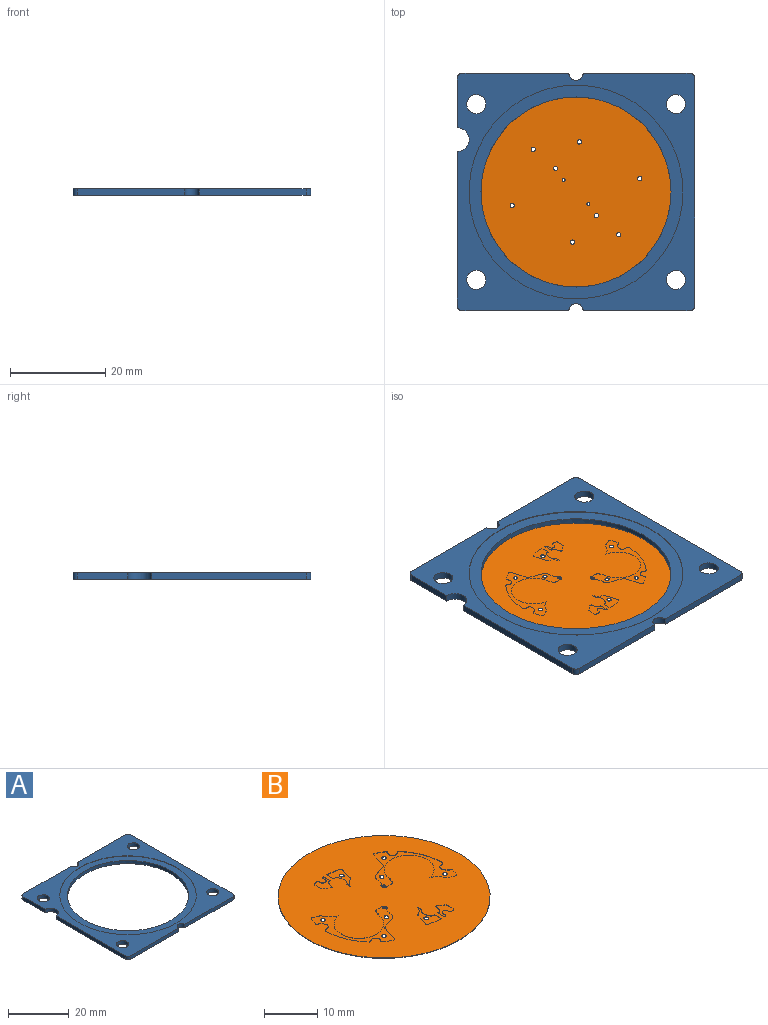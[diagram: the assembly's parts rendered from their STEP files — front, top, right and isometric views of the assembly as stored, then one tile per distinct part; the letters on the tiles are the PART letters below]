
ASSEMBLY  parts=2 mates=1
PART A: 23 faces, bbox 50x50x1.4 mm
  f0: plane 48x1.4mm, normal (1,0,0), area 67.2mm2, adj f1,f17,f18,f19
  f1: cylinder r=1mm len=1.4mm, axis (0,0,-1), area 2.2mm2, adj f0,f2,f18,f19
  f2: plane 22.5x1.4mm, normal (0,1,0), area 31.5mm2, adj f1,f3,f18,f19
  f3: cylinder r=1.5mm len=3mm, axis (0,0,-1), area 6.6mm2, adj f2,f4,f18,f19
  f4: plane 22.5x1.4mm, normal (0,1,0), area 31.5mm2, adj f3,f5,f18,f19
  f5: cylinder r=1mm len=1.4mm, axis (0,0,-1), area 2.2mm2, adj f4,f6,f18,f19
  f6: plane 10.5x1.4mm, normal (-1,0,0), area 14.7mm2, adj f5,f7,f18,f19
  f7: cylinder r=2.5mm len=5mm, axis (0,0,-1), area 11mm2, adj f6,f8,f18,f19
  f8: plane 32.5x1.4mm, normal (-1,0,0), area 45.5mm2, adj f7,f9,f18,f19
  f9: cylinder r=1mm len=1.4mm, axis (0,0,-1), area 2.2mm2, adj f8,f10,f18,f19
  f10: plane 22.5x1.4mm, normal (0,-1,0), area 31.5mm2, adj f9,f11,f18,f19
  f11: cylinder r=1.5mm len=3mm, axis (0,0,-1), area 6.6mm2, adj f10,f12,f18,f19
  f12: plane 22.5x1.4mm, normal (0,-1,0), area 31.5mm2, adj f11,f17,f18,f19
  f13: cylinder r=2mm len=4.01mm, axis (0,0,-1), area 17.6mm2, adj f18,f19
  f14: cylinder r=2mm len=4.01mm, axis (0,0,-1), area 17.6mm2, adj f18,f19
  f15: cylinder r=2mm len=4.01mm, axis (0,0,-1), area 17.6mm2, adj f18,f19
  f16: cylinder r=2mm len=4.01mm, axis (0,0,-1), area 17.6mm2, adj f18,f19
  f17: cylinder r=1mm len=1.4mm, axis (0,0,-1), area 2.2mm2, adj f0,f12,f18,f19
  f18: plane 50x50mm, normal (0,0,1), area 841.3mm2, adj f0,f1,f2,f3,f4,f5,f6,f7
  f19: plane 50x50mm, normal (0,0,-1), area 1175.1mm2, adj f0,f1,f2,f3,f4,f5,f6,f7
  f20: cylinder r=22.5mm len=45mm, axis (0,0,1), area 17mm2, adj f18,f21
  f21: plane 45x45mm, normal (0,0,1), area 333.8mm2, adj f20,f22
  f22: cylinder r=20mm len=40mm, axis (0,0,-1), area 160.8mm2, adj f19,f21
PART B: 127 faces, bbox 40x40x0.1 mm
  f0: plane 40x40mm, normal (0,0,1), area 1136.6mm2, adj f11,f13,f14,f15,f16,f17,f18,f19
  f1: cylinder r=0.45mm len=0.91mm, axis (0,0,1), area 0.1mm2, adj f12,f92
  f2: cylinder r=0.45mm len=0.91mm, axis (0,0,1), area 0.1mm2, adj f12,f92
  f3: cylinder r=0.45mm len=0.89mm, axis (0,0,1), area 0.1mm2, adj f12,f92
  f4: cylinder r=0.3mm len=0.6mm, axis (0,0,1), area 0.1mm2, adj f12,f92
  f5: cylinder r=0.45mm len=0.91mm, axis (0,0,1), area 0.1mm2, adj f12,f63
  f6: cylinder r=0.3mm len=0.6mm, axis (0,0,1), area 0.1mm2, adj f12,f52
  f7: cylinder r=0.45mm len=0.89mm, axis (0,0,1), area 0.1mm2, adj f12,f52
  f8: cylinder r=0.45mm len=0.91mm, axis (0,0,1), area 0.1mm2, adj f12,f52
  f9: cylinder r=0.45mm len=0.91mm, axis (0,0,1), area 0.1mm2, adj f12,f52
  f10: cylinder r=0.45mm len=0.91mm, axis (0,0,1), area 0.1mm2, adj f12,f23
  f11: cylinder r=20mm len=40mm, axis (0,0,-1), area 12.6mm2, adj f0,f12
  f12: plane 40x40mm, normal (0,0,-1), area 1250.9mm2, adj f1,f2,f3,f4,f5,f6,f7,f8
  f13: cylinder r=0.4mm len=0.5mm, axis (0,0,1), area 0mm2, adj f0,f14,f22,f23
  f14: cylinder r=12.7mm len=3.01mm, axis (0,0,1), area 0.2mm2, adj f0,f13,f15,f23
  f15: plane 1.88x0.05mm, normal (1,0,0), area 0.1mm2, adj f0,f14,f16,f23
  f16: cylinder r=0.65mm len=0.91mm, axis (0,0,1), area 0.1mm2, adj f0,f15,f17,f23
  f17: cylinder r=1.65mm len=2.34mm, axis (0,0,1), area 0.1mm2, adj f0,f16,f18,f23
  f18: cylinder r=1.25mm len=0.75mm, axis (0,0,1), area 0mm2, adj f0,f17,f19,f23
  f19: cylinder r=1.25mm len=0.15mm, axis (0,0,1), area 0mm2, adj f0,f18,f20,f23
  f20: cylinder r=2.8mm len=1.64mm, axis (0,0,1), area 0.1mm2, adj f0,f19,f21,f23
  f21: cylinder r=0.6mm len=0.37mm, axis (0,0,1), area 0mm2, adj f0,f20,f22,f23
  f22: plane 2.75x0.85mm, normal (-0.96,0.3,0), area 0.1mm2, adj f0,f13,f21,f23
  f23: plane 5.73x3.3mm, normal (0,0,1), area 9mm2, adj f10,f13,f14,f15,f16,f17,f18,f19
  f24: cylinder r=4.7mm len=9.39mm, axis (0,0,1), area 1mm2, adj f0,f25,f51,f52
  f25: cylinder r=4.7mm len=2.54mm, axis (0,0,1), area 0.2mm2, adj f0,f24,f26,f52
  f26: cylinder r=0.6mm len=0.37mm, axis (0,0,1), area 0mm2, adj f0,f25,f27,f52
  f27: plane 1.09x0.49mm, normal (-0.41,-0.91,0), area 0.1mm2, adj f0,f26,f28,f52
  f28: cylinder r=0.4mm len=0.54mm, axis (0,0,1), area 0mm2, adj f0,f27,f29,f52
  f29: cylinder r=12.7mm len=1.65mm, axis (0,0,1), area 0.1mm2, adj f0,f28,f30,f52
  f30: cylinder r=0.3mm len=0.37mm, axis (0,0,1), area 0mm2, adj f0,f29,f31,f52
  f31: cylinder r=0.5mm len=0.47mm, axis (0,0,1), area 0mm2, adj f0,f30,f32,f52
  f32: plane 0.67x0.39mm, normal (0.86,0.5,0), area 0mm2, adj f0,f31,f33,f52
  f33: cylinder r=0.85mm len=1.28mm, axis (0,0,1), area 0.1mm2, adj f0,f32,f34,f52
  f34: cylinder r=0.5mm len=0.6mm, axis (0,0,1), area 0mm2, adj f0,f33,f35,f52
  f35: cylinder r=12.7mm len=8.29mm, axis (0,0,1), area 0.5mm2, adj f0,f34,f36,f52
  f36: cylinder r=0.3mm len=0.45mm, axis (0,0,1), area 0mm2, adj f0,f35,f37,f52
  f37: cylinder r=0.9mm len=1.58mm, axis (0,0,1), area 0.1mm2, adj f0,f36,f38,f52
  f38: cylinder r=0.3mm len=0.45mm, axis (0,0,1), area 0mm2, adj f0,f37,f39,f52
  f39: cylinder r=12.7mm len=1.81mm, axis (0,0,1), area 0.1mm2, adj f0,f38,f40,f52
  f40: cylinder r=0.4mm len=0.57mm, axis (0,0,1), area 0mm2, adj f0,f39,f41,f52
  f41: plane 3.64x1.14mm, normal (-0.95,0.3,0), area 0.2mm2, adj f0,f40,f42,f52
  f42: cylinder r=0.4mm len=0.26mm, axis (0,0,1), area 0mm2, adj f0,f41,f43,f52
  f43: plane 2.98x1.06mm, normal (-0.34,0.94,0), area 0.2mm2, adj f0,f42,f44,f52
  f44: cylinder r=1.2mm len=1.02mm, axis (0,0,1), area 0.1mm2, adj f0,f43,f45,f52
  f45: cylinder r=5mm len=1.73mm, axis (0,0,1), area 0.1mm2, adj f0,f44,f46,f52
  f46: cylinder r=0.4mm len=0.24mm, axis (0,0,1), area 0mm2, adj f0,f45,f47,f52
  f47: cylinder r=0.6mm len=1.17mm, axis (0,0,1), area 0.1mm2, adj f0,f46,f48,f52
  f48: plane 1.33x0.05mm, normal (0.01,-1,0), area 0.1mm2, adj f0,f47,f49,f52
  f49: cylinder r=0.7mm len=0.67mm, axis (0,0,1), area 0mm2, adj f0,f48,f50,f52
  f50: plane 0.54x0.13mm, normal (0.97,-0.24,0), area 0mm2, adj f0,f49,f51,f52
  f51: cylinder r=0.4mm len=0.27mm, axis (0,0,1), area 0mm2, adj f0,f24,f50,f52
  f52: plane 16.09x13.73mm, normal (0,0,1), area 42mm2, adj f6,f7,f8,f9,f24,f25,f26,f27
  f53: cylinder r=0.4mm len=0.5mm, axis (0,0,1), area 0mm2, adj f0,f54,f62,f63
  f54: cylinder r=12.7mm len=3.01mm, axis (0,0,1), area 0.2mm2, adj f0,f53,f55,f63
  f55: plane 1.88x0.05mm, normal (-1,0,0), area 0.1mm2, adj f0,f54,f56,f63
  f56: cylinder r=0.65mm len=0.91mm, axis (0,0,1), area 0.1mm2, adj f0,f55,f57,f63
  f57: cylinder r=1.65mm len=2.34mm, axis (0,0,1), area 0.1mm2, adj f0,f56,f58,f63
  f58: cylinder r=1.25mm len=0.75mm, axis (0,0,1), area 0mm2, adj f0,f57,f59,f63
  f59: cylinder r=1.25mm len=0.15mm, axis (0,0,1), area 0mm2, adj f0,f58,f60,f63
  f60: cylinder r=2.8mm len=1.64mm, axis (0,0,1), area 0.1mm2, adj f0,f59,f61,f63
  f61: cylinder r=0.6mm len=0.37mm, axis (0,0,1), area 0mm2, adj f0,f60,f62,f63
  f62: plane 2.75x0.85mm, normal (0.96,-0.3,0), area 0.1mm2, adj f0,f53,f61,f63
  f63: plane 5.73x3.3mm, normal (0,0,1), area 9mm2, adj f5,f53,f54,f55,f56,f57,f58,f59
  f64: cylinder r=4.7mm len=9.39mm, axis (0,0,1), area 1mm2, adj f0,f65,f91,f92
  f65: cylinder r=4.7mm len=2.54mm, axis (0,0,1), area 0.2mm2, adj f0,f64,f66,f92
  f66: cylinder r=0.6mm len=0.37mm, axis (0,0,1), area 0mm2, adj f0,f65,f67,f92
  f67: plane 1.09x0.49mm, normal (0.41,0.91,0), area 0.1mm2, adj f0,f66,f68,f92
  f68: cylinder r=0.4mm len=0.54mm, axis (0,0,1), area 0mm2, adj f0,f67,f69,f92
  f69: cylinder r=12.7mm len=1.65mm, axis (0,0,1), area 0.1mm2, adj f0,f68,f70,f92
  f70: cylinder r=0.3mm len=0.37mm, axis (0,0,1), area 0mm2, adj f0,f69,f71,f92
  f71: cylinder r=0.5mm len=0.47mm, axis (0,0,1), area 0mm2, adj f0,f70,f72,f92
  f72: plane 0.67x0.39mm, normal (-0.86,-0.5,0), area 0mm2, adj f0,f71,f73,f92
  f73: cylinder r=0.85mm len=1.28mm, axis (0,0,1), area 0.1mm2, adj f0,f72,f74,f92
  f74: cylinder r=0.5mm len=0.6mm, axis (0,0,1), area 0mm2, adj f0,f73,f75,f92
  f75: cylinder r=12.7mm len=8.29mm, axis (0,0,1), area 0.5mm2, adj f0,f74,f76,f92
  f76: cylinder r=0.3mm len=0.45mm, axis (0,0,1), area 0mm2, adj f0,f75,f77,f92
  f77: cylinder r=0.9mm len=1.58mm, axis (0,0,1), area 0.1mm2, adj f0,f76,f78,f92
  f78: cylinder r=0.3mm len=0.45mm, axis (0,0,1), area 0mm2, adj f0,f77,f79,f92
  f79: cylinder r=12.7mm len=1.81mm, axis (0,0,1), area 0.1mm2, adj f0,f78,f80,f92
  f80: cylinder r=0.4mm len=0.57mm, axis (0,0,1), area 0mm2, adj f0,f79,f81,f92
  f81: plane 3.64x1.14mm, normal (0.95,-0.3,0), area 0.2mm2, adj f0,f80,f82,f92
  f82: cylinder r=0.4mm len=0.26mm, axis (0,0,1), area 0mm2, adj f0,f81,f83,f92
  f83: plane 2.98x1.06mm, normal (0.34,-0.94,0), area 0.2mm2, adj f0,f82,f84,f92
  f84: cylinder r=1.2mm len=1.02mm, axis (0,0,1), area 0.1mm2, adj f0,f83,f85,f92
  f85: cylinder r=5mm len=1.73mm, axis (0,0,1), area 0.1mm2, adj f0,f84,f86,f92
  f86: cylinder r=0.4mm len=0.24mm, axis (0,0,1), area 0mm2, adj f0,f85,f87,f92
  f87: cylinder r=0.6mm len=1.17mm, axis (0,0,1), area 0.1mm2, adj f0,f86,f88,f92
  f88: plane 1.33x0.05mm, normal (-0.01,1,0), area 0.1mm2, adj f0,f87,f89,f92
  f89: cylinder r=0.7mm len=0.67mm, axis (0,0,1), area 0mm2, adj f0,f88,f90,f92
  f90: plane 0.54x0.13mm, normal (-0.97,0.24,0), area 0mm2, adj f0,f89,f91,f92
  f91: cylinder r=0.4mm len=0.27mm, axis (0,0,1), area 0mm2, adj f0,f64,f90,f92
  f92: plane 16.09x13.73mm, normal (0,0,1), area 42mm2, adj f1,f2,f3,f4,f64,f65,f66,f67
  f93: cylinder r=0.6mm len=1.2mm, axis (0,0,1), area 0.1mm2, adj f0,f94,f108,f109
  f94: plane 0.38x0.05mm, normal (0.99,0.13,0), area 0mm2, adj f0,f93,f95,f109
  f95: cylinder r=0.4mm len=0.48mm, axis (0,0,1), area 0mm2, adj f0,f94,f96,f109
  f96: cylinder r=12.7mm len=0.63mm, axis (0,0,1), area 0mm2, adj f0,f95,f97,f109
  f97: cylinder r=0.4mm len=0.44mm, axis (0,0,1), area 0mm2, adj f0,f96,f98,f109
  f98: plane 1.4x0.19mm, normal (-0.99,-0.14,0), area 0.1mm2, adj f0,f97,f99,f109
  f99: cylinder r=0.6mm len=0.3mm, axis (0,0,1), area 0mm2, adj f0,f98,f100,f109
  f100: cylinder r=4.7mm len=1.36mm, axis (0,0,1), area 0.1mm2, adj f0,f99,f101,f109
  f101: cylinder r=2mm len=0.43mm, axis (0,0,1), area 0mm2, adj f0,f100,f102,f109
  f102: cylinder r=1.65mm len=1.01mm, axis (0,0,1), area 0.1mm2, adj f0,f101,f103,f109
  f103: cylinder r=0.65mm len=0.91mm, axis (0,0,1), area 0.1mm2, adj f0,f102,f104,f109
  f104: plane 1.88x0.05mm, normal (1,0,0), area 0.1mm2, adj f0,f103,f105,f109
  f105: cylinder r=12.7mm len=0.19mm, axis (0,0,1), area 0mm2, adj f0,f104,f106,f109
  f106: cylinder r=0.4mm len=0.45mm, axis (0,0,1), area 0mm2, adj f0,f105,f107,f109
  f107: plane 0.38x0.05mm, normal (-0.99,-0.13,0), area 0mm2, adj f0,f106,f108,f109
  f108: plane 0.05x0mm, normal (-0.99,-0.13,0), area 0mm2, adj f0,f93,f107,f109
  f109: plane 3.56x3.16mm, normal (0,0,1), area 6.2mm2, adj f93,f94,f95,f96,f97,f98,f99,f100
  f110: cylinder r=0.6mm len=1.2mm, axis (0,0,1), area 0.1mm2, adj f0,f111,f125,f126
  f111: plane 0.38x0.05mm, normal (-0.99,-0.13,0), area 0mm2, adj f0,f110,f112,f126
  f112: cylinder r=0.4mm len=0.48mm, axis (0,0,1), area 0mm2, adj f0,f111,f113,f126
  f113: cylinder r=12.7mm len=0.63mm, axis (0,0,1), area 0mm2, adj f0,f112,f114,f126
  f114: cylinder r=0.4mm len=0.44mm, axis (0,0,1), area 0mm2, adj f0,f113,f115,f126
  f115: plane 1.4x0.19mm, normal (0.99,0.14,0), area 0.1mm2, adj f0,f114,f116,f126
  f116: cylinder r=0.6mm len=0.3mm, axis (0,0,1), area 0mm2, adj f0,f115,f117,f126
  f117: cylinder r=4.7mm len=1.36mm, axis (0,0,1), area 0.1mm2, adj f0,f116,f118,f126
  f118: cylinder r=2mm len=0.43mm, axis (0,0,1), area 0mm2, adj f0,f117,f119,f126
  f119: cylinder r=1.65mm len=1.01mm, axis (0,0,1), area 0.1mm2, adj f0,f118,f120,f126
  f120: cylinder r=0.65mm len=0.91mm, axis (0,0,1), area 0.1mm2, adj f0,f119,f121,f126
  f121: plane 1.88x0.05mm, normal (-1,0,0), area 0.1mm2, adj f0,f120,f122,f126
  f122: cylinder r=12.7mm len=0.19mm, axis (0,0,1), area 0mm2, adj f0,f121,f123,f126
  f123: cylinder r=0.4mm len=0.45mm, axis (0,0,1), area 0mm2, adj f0,f122,f124,f126
  f124: plane 0.38x0.05mm, normal (0.99,0.13,0), area 0mm2, adj f0,f123,f125,f126
  f125: plane 0.05x0mm, normal (0.99,0.13,0), area 0mm2, adj f0,f110,f124,f126
  f126: plane 3.56x3.16mm, normal (0,0,1), area 6.2mm2, adj f110,f111,f112,f113,f114,f115,f116,f117
PLACE A at identity
PLACE B rot(axis=(1,0,0),180deg) t=(0,0,0.22)mm
MATE fastened B.f11 <-> A.f22  axis (0,0,-1) through (0,0,0.12)mm
